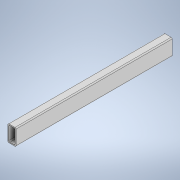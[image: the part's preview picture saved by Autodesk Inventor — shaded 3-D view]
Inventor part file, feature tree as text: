
AUTODESK INVENTOR PART (.ipt)
format: ipt  version: 2020 (Build 240168000, 168)  size: 121,344 bytes
history: native  units: in
note: dims shown in document units (in); Inventor stores cm internally (conversion verified against a paired STEP export)
features: extrude x1, sketch x1
ambient origin geometry x8: Origin, YZ Plane, XZ Plane, XY Plane, X Axis, Y Axis, Z Axis, Center Point
bodies: Solid1 (feature_tree)
feature tree (2):
  extrude  "Extrusion1"  Depth=1.0in
  sketch  "Sketch1"  dims[d0=2.0in d1=1.0in d2=0.125in d3=0.125in d4=0.125in d5=0.125in d6=0.125in d7=0.125in d8=0.125in d9=0.125in d10=0.125in d11=19.0in d12=0.0in]
